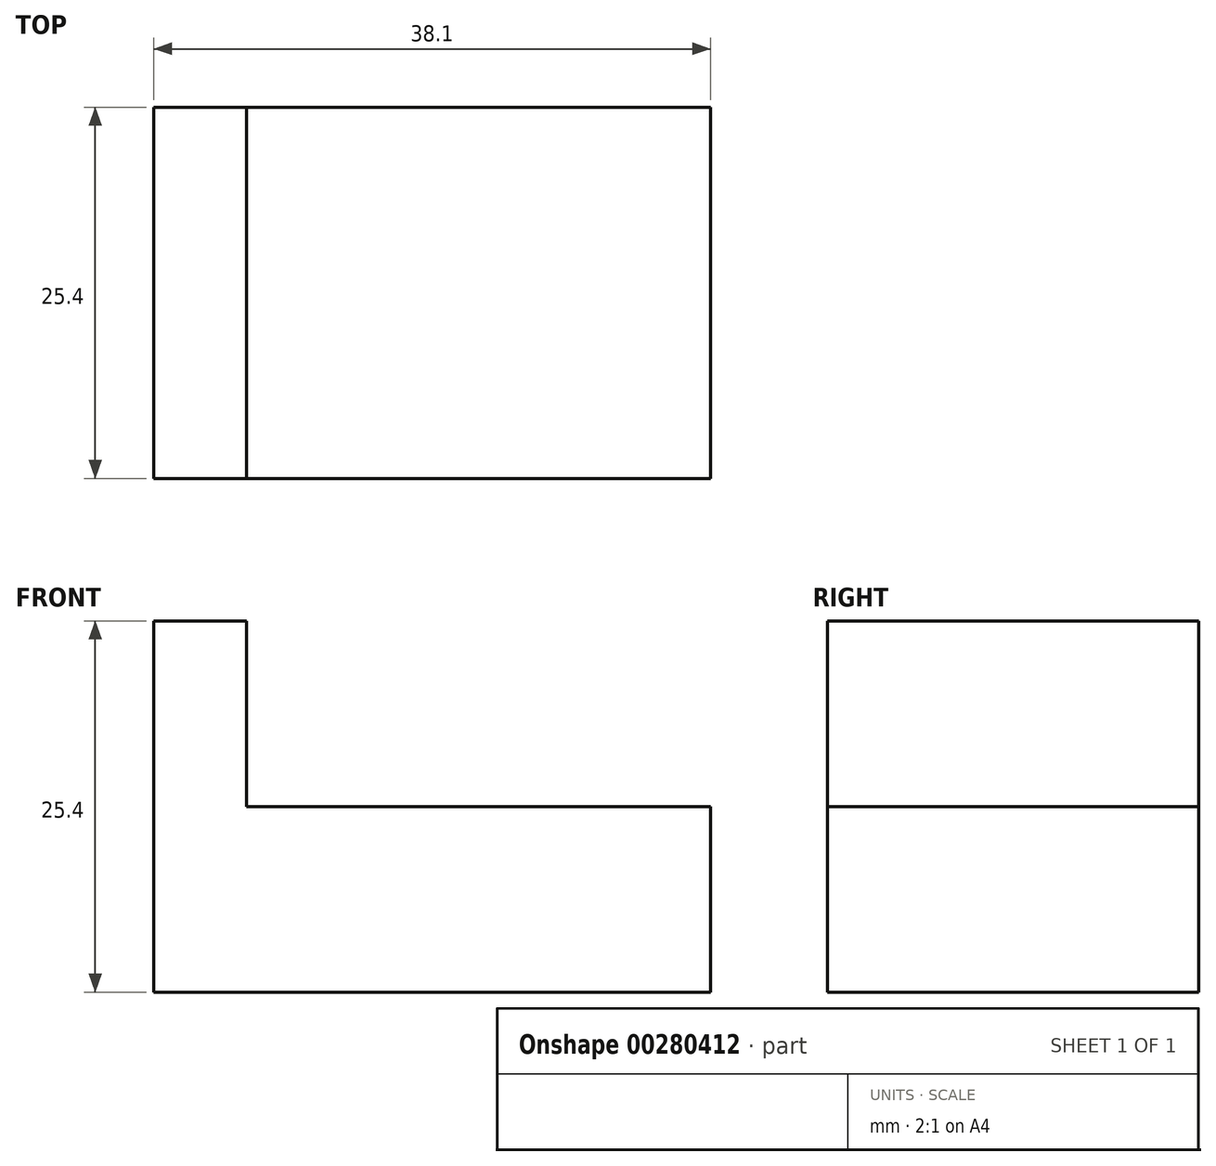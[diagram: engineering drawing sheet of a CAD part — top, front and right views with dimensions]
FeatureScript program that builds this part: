
annotation { "Feature Type Name" : "Feature", "Feature Type Description" : "" }
export const myFeature = defineFeature(function(context is Context, id is Id, definition is map)
    precondition{}
    {
        {
            var Q0;
            Q0=qCreatedBy(makeId("Front.planeOp"),FACE);
            var sketch = newSketch(context, id + "F0", { "sketchPlane" : qUnion([Q0])});
            skLineSegment(sketch, "E0", {"start": v(0, 25.4) * mm, "end": v(0, 0) * mm});
            skLineSegment(sketch, "E1", {"start": v(0, 0) * mm, "end": v(38.1, 0) * mm});
            skLineSegment(sketch, "E2", {"start": v(38.1, 0) * mm, "end": v(38.1, 12.7) * mm});
            skLineSegment(sketch, "E3", {"start": v(38.1, 12.7) * mm, "end": v(6.35, 12.7) * mm});
            skLineSegment(sketch, "E4", {"start": v(6.35, 12.7) * mm, "end": v(6.35, 25.4) * mm});
            skLineSegment(sketch, "E5", {"start": v(6.35, 25.4) * mm, "end": v(0, 25.4) * mm});
            skSolve(sketch);
        }
        {
            var Q0;
            Q0=makeQuery(id+"F0.imprint","IMPRINT",FACE,{"disambiguationData":[TD([[makeQuery(id+"F0.imprint","IMPRINT",EDGE,{"derivedFrom":sQuery(id+"F0.wireOp",EDGE,"E0")}),1.0]])]});
            extrude(context, id + "F1", {"entities" : qUnion([Q0]), "depth" : 25.4 * mm});
        }
    });
